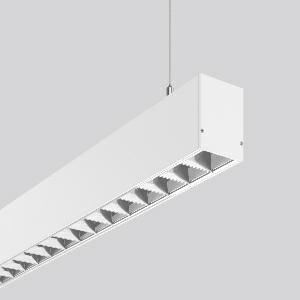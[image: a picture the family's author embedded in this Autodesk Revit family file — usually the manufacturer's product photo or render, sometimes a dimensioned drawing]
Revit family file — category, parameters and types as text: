
# Revit family: less_is_more_50_312343_002_1_76_13d3
name_source: partatom
category: Lighting Fixtures
units: mm (PartAtom-declared; Revit-internal decimal feet)

## family parameters
Cut with Voids When Loaded = No
Host = Face
Light Source = No
Part Type = Normal
Room Calculation Point = No
Round Connector Dimension = Use Diameter
Shared = No

## types (1)
- LESS IS MORE 50 (1 x LED Modul 840, 6700 lm, 4000)
    Apparent Load = 58 VA
    CIE Flux Codes = 95 100 100 63 100
    Color Rendering = 80
    Color Temperature = 4000
    Default Elevation = 1800 mm
    Description = Series: LESS IS MORE 50
Linear pendant luminaire for aesthetically sophisticated lighting. Housing: extruded aluminium profile, powder-coated. End cap aluminium powder-coated. Canopy made of aluminium, powder-coated. Alea optical system: Reflector structure (ABS, Aluminium-coated, highly polished) with integrated diffuser made of non-yellowing plastic (PMMA) opal for glare-free light at the workstation (screen-compliant according to EN 12464-1). Direct 65%, indirect 35% light emission. Controlled separately. Suitable for pendant. 2-point steel cable suspension freely positionable and infinitely height-adjustable. Special lengths available on request. LED unit with integrated converter interchangeable and removable. Suitable for through-wiring. With sensors or as a safety luminaire on request. 
Colour: traffic white, matt (RAL 9016)
Length: 1407 mm
Width: 57 mm
Height: 75 mm
Suspension length: 2000 mm
Lamp: LED
Socket: without socket
Colour temperature: 4000K
Colour rendering index (CRI): 80
Light source: LED
Socket lamp2: Without base
Colour temperature: 4000K
System power: 58 W
Rated luminous flux: 6700 lm
Luminous efficiency: 116 lm/W
Control gear: Converter, dimmable, DALI
Control gear: Converter, dimmable, DALI
Protection class: I
Type of protection: IP 20
    Height = 75 mm
    Lamp = 1 x LED Modul 840
    Lamp Light Flux = 6700 lm
    Lamp count = 1
    Length = 1407 mm
    Lifetime = 50000 h
    Luminous efficacy = 116 lm/W
    Manufacturer = RZB
    ModVariant = No
    Model = 312343.002.1.76
    Mounting Place = Ceiling
    Mounting Type = Pendant
    Number of Poles = 1
    OnlyDefault = Yes
    Power Factor = 1
    Product Name = LESS IS MORE 50
    Product group = Pendant LED linear luminaires
    ProductGroupID = 907
    Protection Class = Protection class I
    Protection Degree = IP 20
    RLX_Detail_Level = 1
    RLX_Emergency_Light_Flux = 0 lm
    RLX_Emergency_Type = 0
    RLX_Emergency_Type_DB = No
    RlxData = <blob elided: 37417 chars, md5=7fcd70d5>
    Socket = socket
    Standby Power = 0 W
    System Light Flux = 6700 lm
    System Power = 58 W
    Type Comments = Product without accessories
    Type Image = 312342.002.jpg
    URL = http://relux.com
    VarID = ---
    Voltage = 230 V
    Voltage Range = 220-240 V
    Weight = 0.00 kg
    Width = 57 mm

## geometry (parser evidence)
native form markers: Blend x4, Sweep x12
no freeform markers — native parametric forms only
